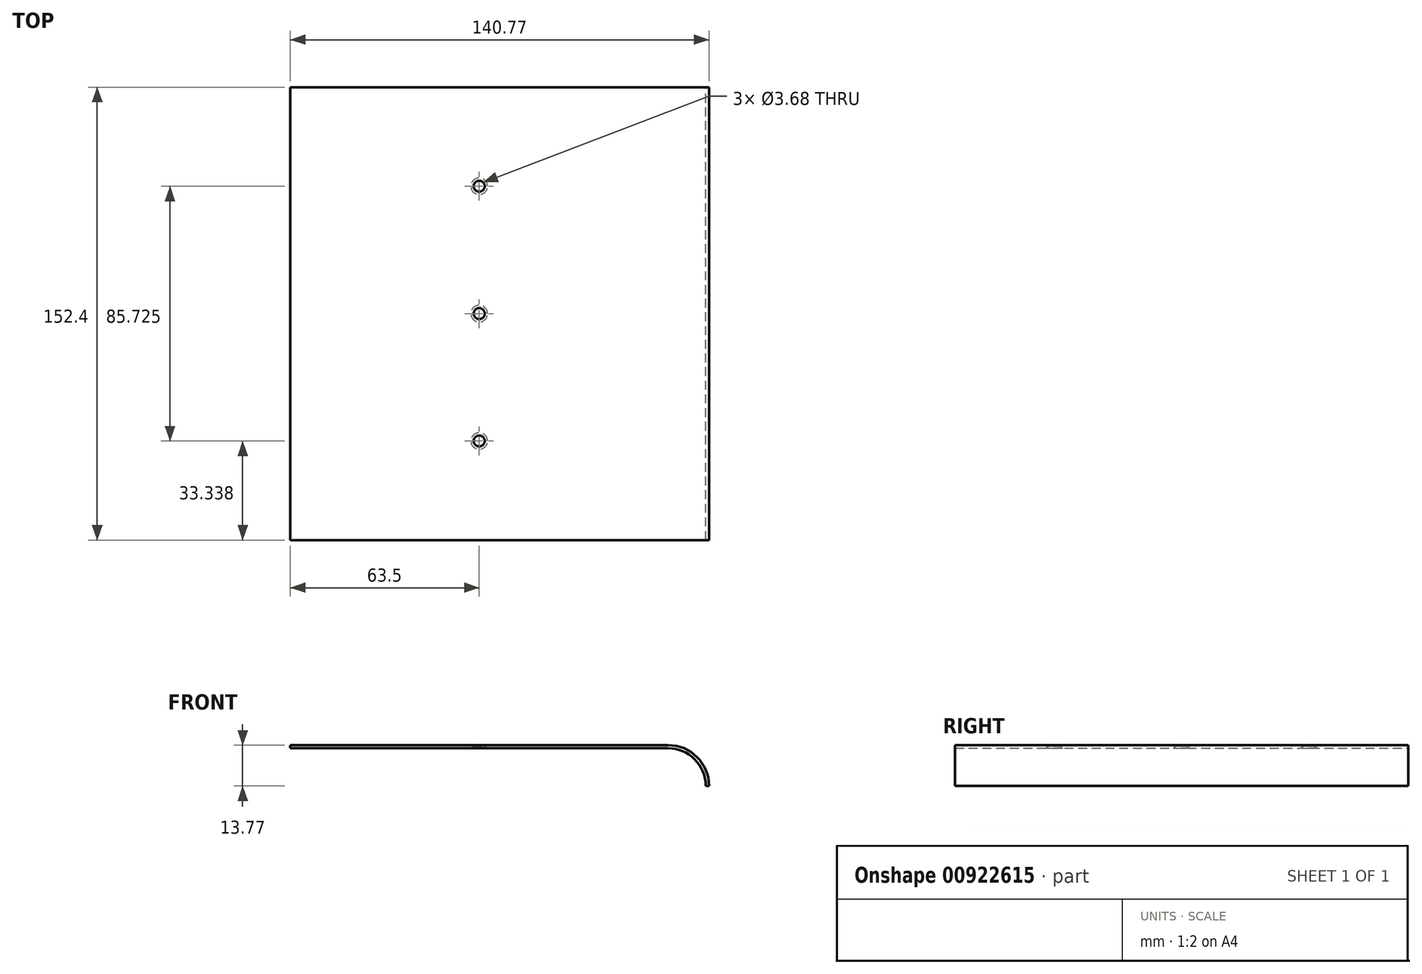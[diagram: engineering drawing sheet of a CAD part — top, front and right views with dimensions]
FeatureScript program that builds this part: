
annotation { "Feature Type Name" : "Feature", "Feature Type Description" : "" }
export const myFeature = defineFeature(function(context is Context, id is Id, definition is map)
    precondition{}
    {
        {
            var Q0;
            Q0=qCreatedBy(makeId("Front.planeOp"),FACE);
            var sketch = newSketch(context, id + "F0", { "sketchPlane" : qUnion([Q0])});
            skLineSegment(sketch, "E0", {"start": v(0, 0) * mm, "end": v(127, 0) * mm});
            skLineSegment(sketch, "E1", {"start": v(139.7, -12.7) * mm, "end": v(139.7, -12.7) * mm});
            skPoint(sketch, "E2.visualSharp", {"position": v(139.7, 0) * mm});
            skArc(sketch, "E2.filletArc", {"start": v(139.7, -12.7) * mm, "mid": v(135.98, -3.72) * mm, "end": v(127, 0) * mm});
            skArc(sketch, "E3.0", {"start": v(140.77, -12.7) * mm, "mid": v(136.73, -2.97) * mm, "end": v(127, 1.07) * mm});
            skLineSegment(sketch, "E3.1", {"start": v(0, 1.07) * mm, "end": v(127, 1.07) * mm});
            skLineSegment(sketch, "E4", {"start": v(0, 0) * mm, "end": v(0, 1.07) * mm});
            skLineSegment(sketch, "E5", {"start": v(139.7, -12.7) * mm, "end": v(140.77, -12.7) * mm});
            skSolve(sketch);
        }
        {
            var Q0;
            Q0 = qSketchRegion(id + "F0", true);
            extrude(context, id + "F1", {"entities" : qUnion([Q0]), "depth" : 76.2 * mm, "offsetDistance" : 25.4 * mm, "hasSecondDirection" : true, "secondDirectionOppositeDirection" : true, "secondDirectionDepth" : 76.2 * mm});
        }
        {
            var Q0;
            Q0=makeQuery(id+"F1.opExtrude","SWEPT_FACE",FACE,{"disambiguationData":[OSD([sQuery(id+"F0.wireOp",EDGE,"E0")])]});
            var sketch = newSketch(context, id + "F2", { "sketchPlane" : qUnion([Q0])});
            skLineSegment(sketch, "E6.0", {"start": v(0, 76.2) * mm, "end": v(0, -76.2) * mm, "construction": true});
            skLineSegment(sketch, "E7.0", {"start": v(127, 76.2) * mm, "end": v(127, -76.2) * mm, "construction": true});
            skLineSegment(sketch, "E8", {"start": v(0, 0) * mm, "end": v(127, 0) * mm, "construction": true});
            skPoint(sketch, "E9", {"position": v(63.5, 0) * mm});
            skPoint(sketch, "E10", {"position": v(63.5, 42.86) * mm});
            skPoint(sketch, "E11", {"position": v(63.5, -42.86) * mm});
            skSolve(sketch);
        }
        {
            var Q0;
            Q0=sQuery(id+"F2.wireOp",VERTEX,"E10");
            var Q1;
            Q1=sQuery(id+"F2.wireOp",VERTEX,"E9");
            var Q2;
            Q2=sQuery(id+"F2.wireOp",VERTEX,"E11");
            var Q3;
            Q3=makeQuery(id+"F1.opExtrude","SWEPT_BODY",BODY,{"disambiguationData":[OSD([sQuery(id+"F0.wireOp",EDGE,"E0"),sQuery(id+"F0.wireOp",EDGE,"E2.filletArc"),sQuery(id+"F0.wireOp",EDGE,"E3.0"),sQuery(id+"F0.wireOp",EDGE,"E3.1"),sQuery(id+"F0.wireOp",EDGE,"E4"),sQuery(id+"F0.wireOp",EDGE,"E5")])]});
            hole(context, id + "F3", {"style" : HoleStyle.C_SINK, "endStyle" : HoleEndStyle.THROUGH, "holeDiameter" : 3.68 * mm, "cSinkDiameter" : 5.6 * mm, "cSinkAngle" : 100 * degree, "majorDiameter" : 6.35 * mm, "tappedDepth" : 12.7 * mm, "tapClearance" : 3, "locations" : qUnion([Q0, Q1, Q2]), "scope" : qUnion([Q3])});
        }
    });
